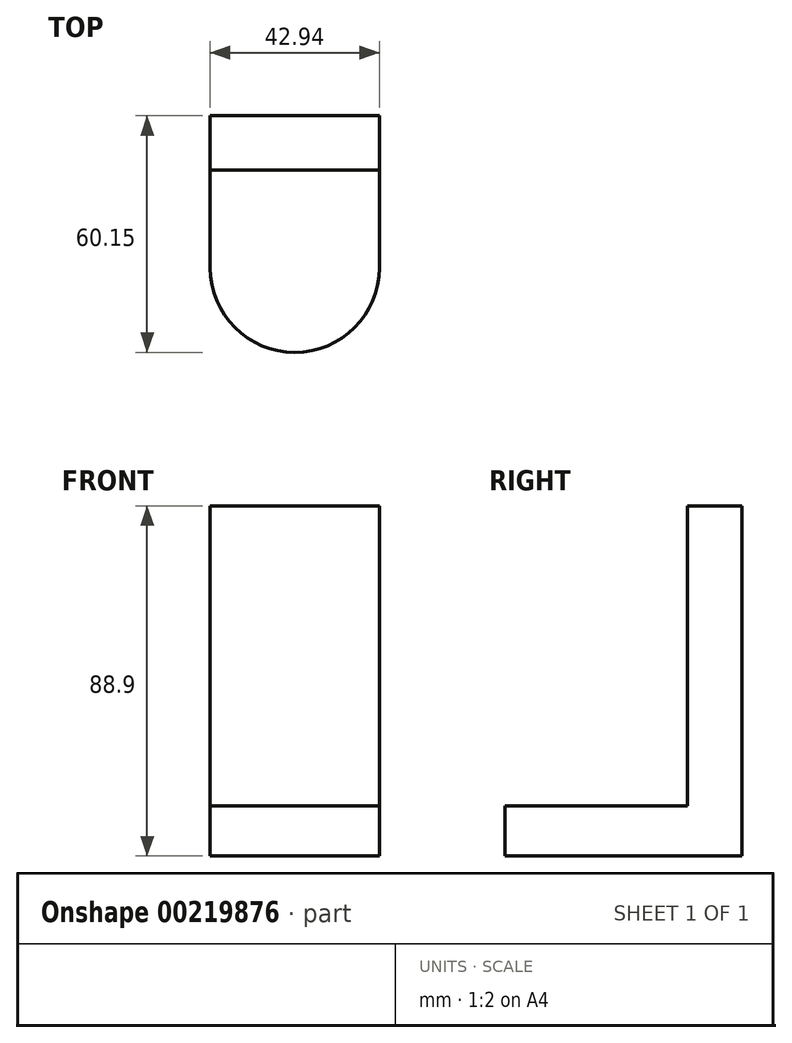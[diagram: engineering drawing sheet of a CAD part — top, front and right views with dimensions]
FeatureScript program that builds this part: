
annotation { "Feature Type Name" : "Feature", "Feature Type Description" : "" }
export const myFeature = defineFeature(function(context is Context, id is Id, definition is map)
    precondition{}
    {
        {
            var Q0;
            Q0=qCreatedBy(makeId("Top.planeOp"),FACE);
            var sketch = newSketch(context, id + "F0", { "sketchPlane" : qUnion([Q0])});
            skLineSegment(sketch, "E0.bottom", {"start": v(21.47, 38.68) * mm, "end": v(-21.47, 38.68) * mm});
            skLineSegment(sketch, "E0.top", {"start": v(21.47, -38.68) * mm, "end": v(-21.47, -38.68) * mm});
            skLineSegment(sketch, "E0.left", {"start": v(21.47, 38.68) * mm, "end": v(21.47, -38.68) * mm});
            skLineSegment(sketch, "E0.right", {"start": v(-21.47, 38.68) * mm, "end": v(-21.47, -38.68) * mm});
            skPoint(sketch, "E0.middle", {"position": v(0, 0) * mm});
            skSolve(sketch);
        }
        {
            var Q0;
            Q0 = qSketchRegion(id + "F0", true);
            extrude(context, id + "F1", {"entities" : qUnion([Q0]), "depth" : 12.7 * mm});
        }
        {
            var Q0;
            Q0=makeQuery(id+"F1.opExtrude","CAP_FACE",FACE,{"disambiguationData":[OSD([sQuery(id+"F0.wireOp",EDGE,"E0.bottom"),sQuery(id+"F0.wireOp",EDGE,"E0.top"),sQuery(id+"F0.wireOp",EDGE,"E0.left"),sQuery(id+"F0.wireOp",EDGE,"E0.right")])],"isStart":false});
            var sketch = newSketch(context, id + "F2", { "sketchPlane" : qUnion([Q0])});
            skArc(sketch, "E1", {"start": v(-21.47, 0) * mm, "mid": v(0, -21.47) * mm, "end": v(21.47, 0) * mm});
            skLineSegment(sketch, "E2", {"start": v(-21.47, 0) * mm, "end": v(-21.47, -38.68) * mm});
            skLineSegment(sketch, "E3", {"start": v(-21.47, -38.68) * mm, "end": v(21.47, -38.68) * mm});
            skLineSegment(sketch, "E4", {"start": v(21.47, -38.68) * mm, "end": v(21.47, 0) * mm});
            skSolve(sketch);
        }
        {
            var Q0;
            Q0=makeQuery(id+"F2.imprint","IMPRINT",FACE,{"disambiguationData":[TD([[makeQuery(id+"F2.imprint","IMPRINT",EDGE,{"derivedFrom":sQuery(id+"F2.wireOp",EDGE,"E1")}),-1.0]])]});
            extrude(context, id + "F3", {"entities" : qUnion([Q0]), "operationType" : NewBodyOperationType.REMOVE, "oppositeDirection" : true, "depth" : 25.4 * mm});
        }
        {
            var Q0;
            Q0=makeQuery(id+"F1.opExtrude","CAP_FACE",FACE,{"disambiguationData":[OSD([sQuery(id+"F0.wireOp",EDGE,"E0.bottom"),sQuery(id+"F0.wireOp",EDGE,"E0.top"),sQuery(id+"F0.wireOp",EDGE,"E0.left"),sQuery(id+"F0.wireOp",EDGE,"E0.right")])],"isStart":false});
            var sketch = newSketch(context, id + "F4", { "sketchPlane" : qUnion([Q0])});
            skLineSegment(sketch, "E5.bottom", {"start": v(-21.47, 38.68) * mm, "end": v(21.47, 38.68) * mm});
            skLineSegment(sketch, "E5.top", {"start": v(-21.47, 24.82) * mm, "end": v(21.47, 24.82) * mm});
            skLineSegment(sketch, "E5.left", {"start": v(-21.47, 38.68) * mm, "end": v(-21.47, 24.82) * mm});
            skLineSegment(sketch, "E5.right", {"start": v(21.47, 38.68) * mm, "end": v(21.47, 24.82) * mm});
            skSolve(sketch);
        }
        {
            var Q0;
            Q0 = qSketchRegion(id + "F4", true);
            extrude(context, id + "F5", {"entities" : qUnion([Q0]), "operationType" : NewBodyOperationType.ADD, "depth" : 76.2 * mm});
        }
    });
